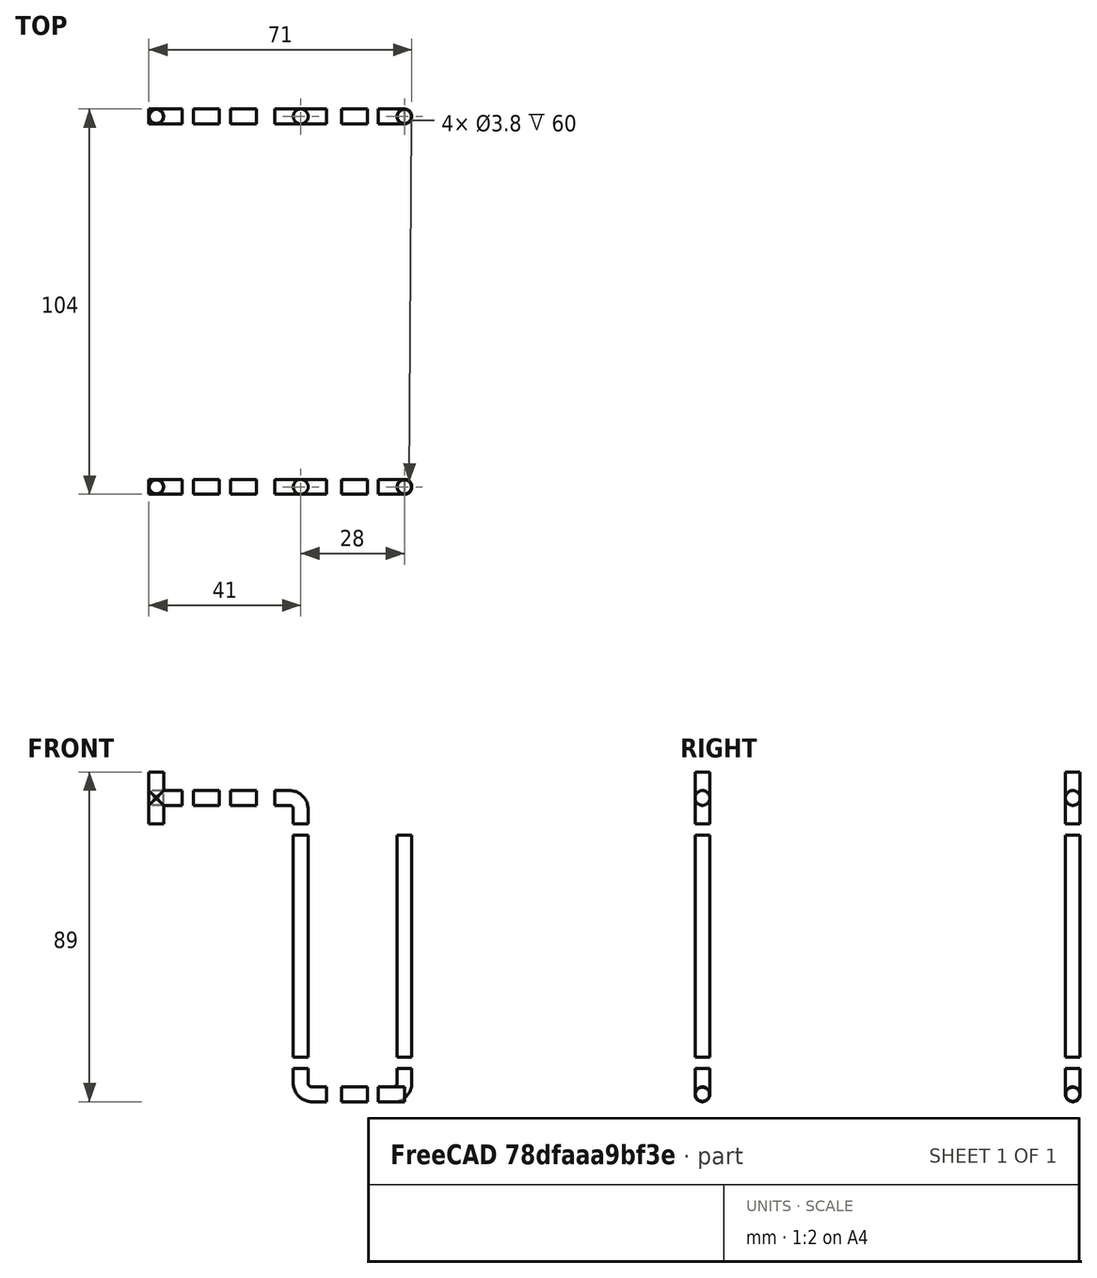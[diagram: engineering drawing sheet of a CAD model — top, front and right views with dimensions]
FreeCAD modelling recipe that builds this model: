
FCSTD DOCUMENT  (FreeCAD 0.21R33771 (Git))
Label: 20240721_SurfCarry
License: All rights reserved
LicenseURL: https://en.wikipedia.org/wiki/All_rights_reserved
objects: Part::Feature×14, PartDesign::Body×7, PartDesign::FeatureBase×6, Sketcher::SketchObject×2, PartDesign::AdditivePipe×1
note: 31 computed .brp shape members not serialized (recipe doc carries the construction recipe); baked Part::Feature solids carry a one-line shape summary decoded from their .brp

FEATURE [Part::Feature] TShape1
  Placement = pos=(0,0,0) rot=(0,1,0;4.71239rad)
  shape: bbox 9 x 4 x 14 mm, 27 faces (baked)
FEATURE [Part::Feature] TShape2
  Placement = pos=(0,100,0) rot=(0,1,0;4.71239rad)
  shape: bbox 9 x 4 x 14 mm, 27 faces (baked)
FEATURE [Part::Feature] Cilindrito1
  Placement = pos=(20,0,0) rot=(0,1,0;4.71239rad)
  shape: bbox 7 x 4 x 4 mm, 4 faces (baked)
FEATURE [Part::Feature] Cilindrito2
  Placement = pos=(50,0,-80) rot=(0,1,0;4.71239rad)
  shape: bbox 7 x 4 x 4 mm, 4 faces (baked)
FEATURE [Part::Feature] Cilindrito3
  Placement = pos=(20,100,0) rot=(0,1,0;4.71239rad)
  shape: bbox 7 x 4 x 4 mm, 4 faces (baked)
FEATURE [Part::Feature] Cilindrito4
  Placement = pos=(50,100,-80) rot=(0,1,0;4.71239rad)
  shape: bbox 7 x 4 x 4 mm, 4 faces (baked)
FEATURE [Part::Feature] CilindritoAserruchado1
  Placement = pos=(10,0,0) rot=(0,1,0;4.71239rad)
  shape: bbox 7 x 4 x 4 mm, 4 faces (baked)
FEATURE [Part::Feature] CilindritoAserruchado2
  Placement = pos=(60,0,-80) rot=(0,1,0;4.71239rad)
  shape: bbox 7 x 4 x 4 mm, 4 faces (baked)
FEATURE [Part::Feature] CilindritoAserruchado3
  Placement = pos=(10,100,0) rot=(0,1,0;4.71239rad)
  shape: bbox 7 x 4 x 4 mm, 4 faces (baked)
FEATURE [Part::Feature] CilindritoAserruchado4
  Placement = pos=(60,100,-80) rot=(0,1,0;4.71239rad)
  shape: bbox 7 x 4 x 4 mm, 4 faces (baked)
FEATURE [Part::Feature] CilindroGrande1
  Placement = pos=(32,0,-70) rot=(0,0,1;0rad)
  shape: bbox 4 x 4 x 60 mm, 4 faces (baked)
FEATURE [Part::Feature] CilindroGrande2
  Placement = pos=(60,0,-70) rot=(0,0,1;0rad)
  shape: bbox 4 x 4 x 60 mm, 4 faces (baked)
FEATURE [Part::Feature] CilindroGrande3
  Placement = pos=(32,100,-70) rot=(0,0,1;0rad)
  shape: bbox 4 x 4 x 60 mm, 4 faces (baked)
FEATURE [Part::Feature] CilindroGrande4
  Placement = pos=(60,100,-70) rot=(0,0,1;0rad)
  shape: bbox 4 x 4 x 60 mm, 4 faces (baked)
FEATURE [Sketcher::SketchObject] Sketch
  FullyConstrained = false
  MapMode = 5
  Support = -> [XY_Plane]
  sketch-geometry (1):
    g0: Circle CenterX=0 CenterY=0 CenterZ=0 NormalX=0 NormalY=0 NormalZ=1 AngleXU=0 Radius=2
  constraints (1):
    c: Coincident(g0,g-1)
FEATURE [Sketcher::SketchObject] Sketch001
  FullyConstrained = false
  MapMode = 5
  Placement = pos=(0,0,0) rot=(1,0,0;1.5708rad)
  Support = -> [XZ_Plane]
  sketch-geometry (3):
    g0: LineSegment StartX=0 StartY=0 StartZ=0 EndX=0 EndY=4 EndZ=0
    g1: LineSegment StartX=3 StartY=7 StartZ=0 EndX=7 EndY=7 EndZ=0
    g2: ArcOfCircle CenterX=3 CenterY=4 CenterZ=0 NormalX=0 NormalY=0 NormalZ=1 AngleXU=0 Radius=3 StartAngle=1.5708 EndAngle=3.14159
  constraints (4):
    c: Coincident(g-1,g0)
    c: Horizontal(g1)
    c: Tangent(g1,g2) = 1.5708
    c: Tangent(g0,g2) = 1.5708
FEATURE [PartDesign::AdditivePipe] AdditivePipe
  AuxilleryCurvelinear = true
  AuxillerySpineTangent = false
  Binormal = (0,0,0)
  Mode = 0
  Profile = -> Sketch
  Spine = -> Sketch001
  SpineTangent = false
  Transformation = 0
  Transition = 0
FEATURE [PartDesign::Body] BodyOriginal
  Group = -> [Sketch,Sketch001,AdditivePipe]
  Origin = -> Origin
  Tip = -> AdditivePipe
FEATURE [PartDesign::FeatureBase] Clone1
  BaseFeature = -> BodyOriginal
FEATURE [PartDesign::Body] Body1
  Group = -> [Clone1]
  Origin = -> Origin001
  Placement = pos=(25,0,0) rot=(0,1,0;1.5708rad)
  Tip = -> Clone1
FEATURE [PartDesign::FeatureBase] Clone2
  BaseFeature = -> BodyOriginal
FEATURE [PartDesign::Body] Body2
  Group = -> [Clone2]
  Origin = -> Origin002
  Placement = pos=(39,0,-80) rot=(0,1,0;4.71239rad)
  Tip = -> Clone2
FEATURE [PartDesign::FeatureBase] Clone3
  BaseFeature = -> BodyOriginal
FEATURE [PartDesign::Body] Body3
  Group = -> [Clone3]
  Origin = -> Origin003
  Placement = pos=(53,0,-80) rot=(0.707107,0,0.707107;3.14159rad)
  Tip = -> Clone3
FEATURE [PartDesign::FeatureBase] Clone4
  BaseFeature = -> BodyOriginal
FEATURE [PartDesign::Body] Body4
  Group = -> [Clone4]
  Origin = -> Origin004
  Placement = pos=(25,100,0) rot=(0,1,0;1.5708rad)
  Tip = -> Clone4
FEATURE [PartDesign::FeatureBase] Clone5
  BaseFeature = -> BodyOriginal
FEATURE [PartDesign::Body] Body5
  Group = -> [Clone5]
  Origin = -> Origin005
  Placement = pos=(39,100,-80) rot=(0,1,0;4.71239rad)
  Tip = -> Clone5
FEATURE [PartDesign::FeatureBase] Clone6
  BaseFeature = -> BodyOriginal
FEATURE [PartDesign::Body] Body6
  Group = -> [Clone6]
  Origin = -> Origin006
  Placement = pos=(53,100,-80) rot=(0.707107,0,0.707107;3.14159rad)
  Tip = -> Clone6
